# Revit family: Window-All_Weather-Series_6100-Fixed
name_source: partatom
category: Windows
units: mm (PartAtom-declared; Revit-internal decimal feet)

## family parameters
Always vertical = Yes
Classification Number = 23.30.20.17.11
Cut with Voids When Loaded = No
Host = Wall
Room Calculation Point = No
Shared = No

## types (1)
- Nail On Frame Fixed
    Assembly Code = B2020110
    CD_Finish = Metal-Aluminum-All_Weather-Anodized-Clear-Class_I
    CD_Finish Glass = Glass-All_Weather-OA-Insulated_Glass
    CD_Glass Inset = 0' - 0 29/32"
    CD_Glass Offset = 0' - 2 3/8"
    CD_Glass Thickness = 0' - 1"
    CD_Grille Horizontal Length = 3' - 0"
    CD_Grille Horizontal Offset = 0' - 10 1/8"
    CD_Grille Size = 0' - 3 3/16"
    CD_Grille Standard = No
    CD_Grille Vertical Length = 3' - 0"
    CD_Grille Vertical Offset = 0' - 10 1/8"
    CD_Head Height = 0' - 2"
    CD_Height = 3' - 0"
    CD_Height Max = 8' - 0"
    CD_Height Min = 0' - 8"
    CD_Inset = 0' - 0"
    CD_Jamb Extension = No
    CD_Jamb Width = 0' - 2"
    CD_Lites Standard High = 2
    CD_Lites Standard Wide = 2
    CD_Microsite = https://microsite.caddetails.com
    CD_Offset = 0' - 0"
    CD_Offset Mounting = 0' - 0 1/16"
    CD_Product Documentation Link = https://www.allweatheraa.com
    CD_Product Name = Series 6100
    CD_Product Page URL = https://www.allweatheraa.com
    CD_Requested Height = 3' - 0"
    CD_Requested Width = 3' - 0"
    CD_Sill Height = 0' - 2"
    CD_Thickness = 0' - 3 25/32"
    CD_Vis Grille Horiontal Single = No
    CD_Vis Grille Horizontal Array = No
    CD_Vis Grille Vertical Array = No
    CD_Vis Grille Vertical Single = No
    CD_Vis Lites Max = 10
    CD_Vis Mullions Horizontal = 2
    CD_Vis Mullions Vertical = 2
    CD_Warranty = https://www.allweatheraa.com
    CD_Width = 3' - 0"
    CD_Width Max = 4' - 0"
    CD_Width Min = 0' - 8"
    Default Sill Height = 3' - 0"
    Description = 3 3/4 in Thermally Optimized Window System
    Height = 3' - 0"
    Manufacturer = All Weather Architectural Aluminum
    Model = Fixed
    Operation = Fixed
    Rough Height = 3' - 0 3/4"
    Rough Width = 3' - 0 3/4"
    Type Comments = Standard Nail On Frame
    URL = https://www.allweatheraa.com
    Wall Closure = By host
    Width = 3' - 0"

## geometry (parser evidence)
native form markers: Sweep x4
no freeform markers — native parametric forms only
